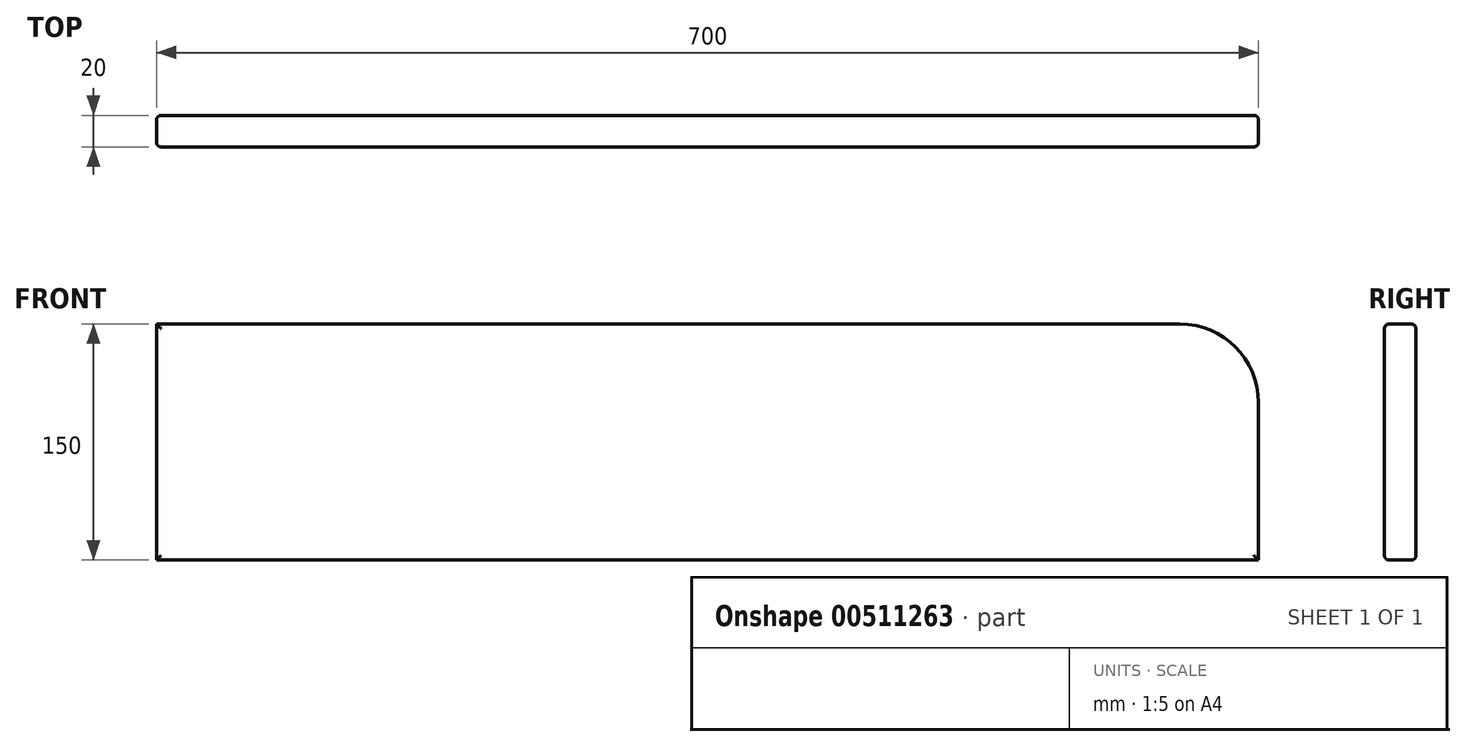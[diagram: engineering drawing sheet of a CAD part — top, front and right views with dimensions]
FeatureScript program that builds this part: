
annotation { "Feature Type Name" : "Feature", "Feature Type Description" : "" }
export const myFeature = defineFeature(function(context is Context, id is Id, definition is map)
    precondition{}
    {
        {
            var Q0;
            Q0=qCreatedBy(makeId("Front.planeOp"),FACE);
            var sketch = newSketch(context, id + "F0", { "sketchPlane" : qUnion([Q0])});
            skLineSegment(sketch, "E0.bottom", {"start": v(-149.82, 70.41) * mm, "end": v(500.18, 70.41) * mm});
            skLineSegment(sketch, "E0.top", {"start": v(-149.82, -79.59) * mm, "end": v(550.18, -79.59) * mm});
            skLineSegment(sketch, "E0.left", {"start": v(-149.82, 70.41) * mm, "end": v(-149.82, -79.59) * mm});
            skLineSegment(sketch, "E0.right", {"start": v(550.18, 20.41) * mm, "end": v(550.18, -79.59) * mm});
            skPoint(sketch, "E1.visualSharp", {"position": v(550.18, 70.41) * mm});
            skArc(sketch, "E1.filletArc", {"start": v(550.18, 20.41) * mm, "mid": v(535.53, 55.77) * mm, "end": v(500.18, 70.41) * mm});
            skSolve(sketch);
        }
        {
            var Q0;
            Q0=makeQuery(id+"F0.imprint","IMPRINT",FACE,{"disambiguationData":[TD([[makeQuery(id+"F0.imprint","IMPRINT",EDGE,{"derivedFrom":sQuery(id+"F0.wireOp",EDGE,"E0.bottom")}),-1.0]])]});
            extrude(context, id + "F1", {"entities" : qUnion([Q0]), "depth" : 20 * mm});
        }
        {
            var Q0;
            Q0=makeQuery(id+"F1.opExtrude","CAP_FACE",FACE,{"disambiguationData":[OSD([sQuery(id+"F0.wireOp",EDGE,"E0.bottom"),sQuery(id+"F0.wireOp",EDGE,"E0.top"),sQuery(id+"F0.wireOp",EDGE,"E0.left"),sQuery(id+"F0.wireOp",EDGE,"E0.right"),sQuery(id+"F0.wireOp",EDGE,"E1.filletArc")])],"isStart":false});
            var sketch = newSketch(context, id + "F2", { "sketchPlane" : qUnion([Q0])});
            skLineSegment(sketch, "E2", {"start": v(-149.82, -79.59) * mm, "end": v(-134.82, -79.59) * mm});
            skLineSegment(sketch, "E3", {"start": v(-134.82, -79.59) * mm, "end": v(-134.82, -49.59) * mm});
            skLineSegment(sketch, "E4", {"start": v(-149.82, -79.59) * mm, "end": v(-149.82, -49.59) * mm});
            skLineSegment(sketch, "E5", {"start": v(-149.82, -49.59) * mm, "end": v(-134.82, -49.59) * mm});
            skLineSegment(sketch, "E6", {"start": v(-134.82, -49.59) * mm, "end": v(-102.82, -49.59) * mm});
            skLineSegment(sketch, "E7", {"start": v(-134.82, -49.59) * mm, "end": v(-134.82, 70.41) * mm});
            skLineSegment(sketch, "E8", {"start": v(-102.82, -49.59) * mm, "end": v(457.18, -49.59) * mm});
            skLineSegment(sketch, "E9", {"start": v(457.18, -49.59) * mm, "end": v(550.18, -49.59) * mm});
            skSolve(sketch);
        }
        {
            var Q0;
            Q0=makeQuery(id+"F1.opExtrude","CAP_FACE",FACE,{"disambiguationData":[OSD([sQuery(id+"F0.wireOp",EDGE,"E0.bottom"),sQuery(id+"F0.wireOp",EDGE,"E0.top"),sQuery(id+"F0.wireOp",EDGE,"E0.left"),sQuery(id+"F0.wireOp",EDGE,"E0.right"),sQuery(id+"F0.wireOp",EDGE,"E1.filletArc")])],"isStart":true});
            var sketch = newSketch(context, id + "F3", { "sketchPlane" : qUnion([Q0])});
            skLineSegment(sketch, "E10", {"start": v(-550.18, -49.59) * mm, "end": v(-457.51, -49.59) * mm});
            skLineSegment(sketch, "E11", {"start": v(134.49, -49.59) * mm, "end": v(134.49, -79.59) * mm});
            skLineSegment(sketch, "E12", {"start": v(-457.51, -49.59) * mm, "end": v(102.49, -49.59) * mm});
            skLineSegment(sketch, "E13", {"start": v(102.49, -49.59) * mm, "end": v(134.49, -49.59) * mm});
            skSolve(sketch);
        }
        {
            var Q0;
            Q0=makeQuery(id+"F1.opExtrude","CAP_FACE",FACE,{"disambiguationData":[OSD([sQuery(id+"F0.wireOp",EDGE,"E0.bottom"),sQuery(id+"F0.wireOp",EDGE,"E0.top"),sQuery(id+"F0.wireOp",EDGE,"E0.left"),sQuery(id+"F0.wireOp",EDGE,"E0.right"),sQuery(id+"F0.wireOp",EDGE,"E1.filletArc")])],"isStart":true});
            var Q1;
            Q1=makeQuery(id+"F1.opExtrude","CAP_FACE",FACE,{"disambiguationData":[OSD([sQuery(id+"F0.wireOp",EDGE,"E0.bottom"),sQuery(id+"F0.wireOp",EDGE,"E0.top"),sQuery(id+"F0.wireOp",EDGE,"E0.left"),sQuery(id+"F0.wireOp",EDGE,"E0.right"),sQuery(id+"F0.wireOp",EDGE,"E1.filletArc")])],"isStart":false});
            fillet(context, id + "F4", {"entities" : qUnion([Q0, Q1]), "radius" : 3 * mm, "tangentPropagation" : true, "allowEdgeOverflow" : false});
        }
    });
